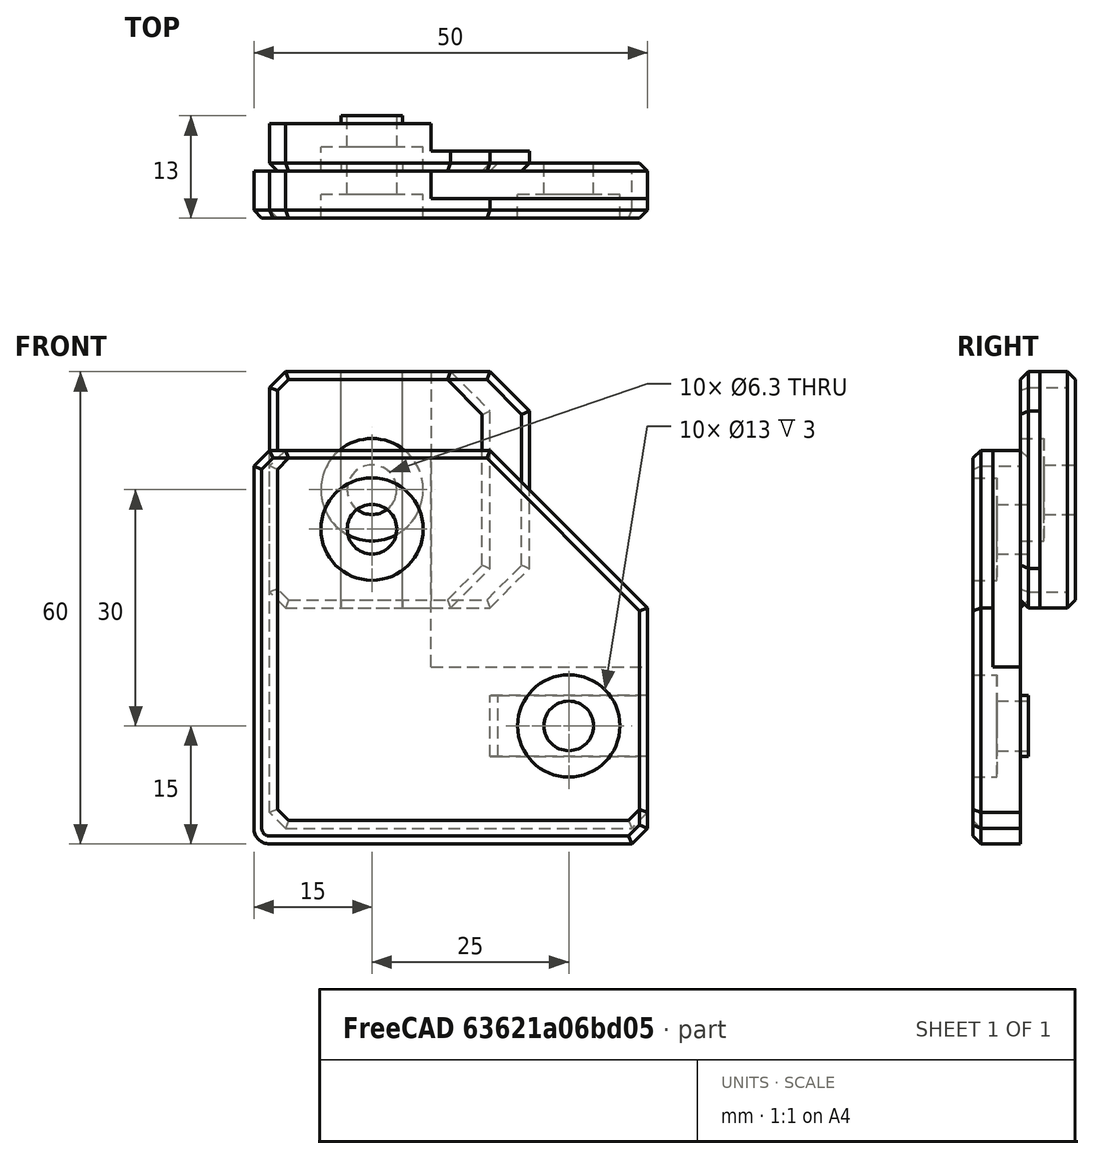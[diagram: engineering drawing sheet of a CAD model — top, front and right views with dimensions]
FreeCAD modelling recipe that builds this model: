
FCSTD DOCUMENT  (FreeCAD 0.19R24291 (Git))
Label: side-top-panel-clip
License: Other
LicenseURL: GPL3
objects: Part::Chamfer×14, Part::Box×11, Part::Cylinder×10, Part::MultiFuse×9, Part::Cut×9, Part::Feature×5, Part::Fillet×1, Part::Refine×1
note: 60 computed .brp shape members not serialized (recipe doc carries the construction recipe); baked Part::Feature solids carry a one-line shape summary decoded from their .brp

FEATURE [Part::Box] Box  label="Cube"
  AttacherType = Attacher::AttachEngine3D
  Height = 48
  Length = 48
  Placement = pos=(-28,-6,-28) rot=(0,0,1;0rad)
  Width = 6
FEATURE [Part::Box] Box001  label="Cube001"
  AttacherType = Attacher::AttachEngine3D
  Height = 20
  Length = 7.8
  Placement = pos=(-18.9,-1,0) rot=(0,0,1;0rad)
  Width = 2
FEATURE [Part::Chamfer] Chamfer
  Base = -> Box
  Edges = 1 edges r=20: [Edge6]
FEATURE [Part::Chamfer] Chamfer001
  Base = -> Chamfer
  Edges = 3 edges r=2: [Edge3,Edge11,Edge15]
FEATURE [Part::Chamfer] Chamfer002
  Base = -> Chamfer001
  Edges = 8 edges r=1: [Edge1,Edge5,Edge6,Edge7,Edge8,Edge9,Edge10,Edge11]
FEATURE [Part::Cylinder] Cylinder
  Angle = 360
  AttacherType = Attacher::AttachEngine3D
  Height = 10
  Placement = pos=(-15,-7,10) rot=(-1,0,0;1.5708rad)
  Radius = 3.15
FEATURE [Part::Cylinder] Cylinder001
  Angle = 360
  AttacherType = Attacher::AttachEngine3D
  Height = 10
  Placement = pos=(10,-7,-15) rot=(-1,0,0;1.5708rad)
  Radius = 3.15
FEATURE [Part::Box] Box002  label="Cube002"
  AttacherType = Attacher::AttachEngine3D
  Height = 7.8
  Length = 20
  Placement = pos=(0,-1,-18.9) rot=(0,0,1;0rad)
  Width = 2
FEATURE [Part::Chamfer] Chamfer003
  Base = -> Box001
  Edges = 2 edges r=1: [Edge11,Edge12]
FEATURE [Part::Chamfer] Chamfer004
  Base = -> Box002
  Edges = 2 edges r=1: [Edge3,Edge7]
FEATURE [Part::MultiFuse] Fusion
  Shapes = -> [Chamfer004,Chamfer003]
FEATURE [Part::MultiFuse] Fusion001
  Shapes = -> [Chamfer002,Fusion]
FEATURE [Part::Cylinder] Cylinder002
  Angle = 360
  AttacherType = Attacher::AttachEngine3D
  Height = 10
  Placement = pos=(10,-16,-15) rot=(-1,0,0;1.5708rad)
  Radius = 6.5
FEATURE [Part::Cylinder] Cylinder003
  Angle = 360
  AttacherType = Attacher::AttachEngine3D
  Height = 10
  Placement = pos=(-15,-16,10) rot=(-1,0,0;1.5708rad)
  Radius = 6.5
FEATURE [Part::MultiFuse] Fusion002
  Shapes = -> [Cylinder,Cylinder001]
FEATURE [Part::Cut] Cut
  Base = -> Fusion001
  Tool = -> Fusion002
FEATURE [Part::MultiFuse] Fusion003
  Placement = pos=(0,3,0) rot=(0,0,1;0rad)
  Shapes = -> [Cylinder003,Cylinder002]
FEATURE [Part::Cut] Cut001
  Base = -> Cut
  Tool = -> Fusion003
FEATURE [Part::Box] Box003  label="Cube003"
  AttacherType = Attacher::AttachEngine3D
  Height = 28
  Length = 28
  Placement = pos=(-7.5,-3.5,-7.5) rot=(0,0,1;0rad)
  Width = 16
FEATURE [Part::Feature] Cut002001  label="panel-mount001"
  shape: bbox 48 x 7 x 48 mm, 37 faces (baked)
FEATURE [Part::Box] Box004  label="Cube004"
  AttacherType = Attacher::AttachEngine3D
  Height = 30
  Length = 28
  Placement = pos=(-28,0,0) rot=(0,0,1;0rad)
  Width = 6
FEATURE [Part::Cylinder] Cylinder004
  Angle = 360
  AttacherType = Attacher::AttachEngine3D
  Height = 10
  Placement = pos=(-15,-7,15) rot=(-1,0,0;1.5708rad)
  Radius = 6.5
FEATURE [Part::Cylinder] Cylinder005
  Angle = 360
  AttacherType = Attacher::AttachEngine3D
  Height = 10
  Placement = pos=(-15,3e-15,15) rot=(-1,0,0;1.5708rad)
  Radius = 3.15
FEATURE [Part::Box] Box005  label="Cube005"
  AttacherType = Attacher::AttachEngine3D
  Height = 31
  Length = 16
  Placement = pos=(-7.5,2.5,0) rot=(0,0,1;0rad)
  Width = 9
FEATURE [Part::Box] Box006  label="Cube006"
  AttacherType = Attacher::AttachEngine3D
  Height = 30
  Length = 7.8
  Placement = pos=(-18.9,5,0) rot=(0,0,1;0rad)
  Width = 2
FEATURE [Part::Chamfer] Chamfer008
  Base = -> Box006
  Edges = 2 edges r=1: [Edge11,Edge12]
FEATURE [Part::Cylinder] Cylinder006
  Angle = 360
  AttacherType = Attacher::AttachEngine3D
  Height = 10
  Placement = pos=(10,-16,-15) rot=(-1,0,0;1.5708rad)
  Radius = 6.5
FEATURE [Part::Box] Box007  label="Cube007"
  AttacherType = Attacher::AttachEngine3D
  Height = 20
  Length = 7.8
  Placement = pos=(-18.9,-1,0) rot=(0,0,1;0rad)
  Width = 2
FEATURE [Part::Cylinder] Cylinder007
  Angle = 360
  AttacherType = Attacher::AttachEngine3D
  Height = 10
  Placement = pos=(-15,-16,10) rot=(-1,0,0;1.5708rad)
  Radius = 6.5
FEATURE [Part::Cylinder] Cylinder008
  Angle = 360
  AttacherType = Attacher::AttachEngine3D
  Height = 10
  Placement = pos=(-15,-7,10) rot=(-1,0,0;1.5708rad)
  Radius = 3.15
FEATURE [Part::Cylinder] Cylinder009
  Angle = 360
  AttacherType = Attacher::AttachEngine3D
  Height = 10
  Placement = pos=(10,-7,-15) rot=(-1,0,0;1.5708rad)
  Radius = 3.15
FEATURE [Part::Chamfer] Chamfer010
  Base = -> Box007
  Edges = 2 edges r=1: [Edge11,Edge12]
FEATURE [Part::Box] Box008  label="Cube008"
  AttacherType = Attacher::AttachEngine3D
  Height = 50
  Length = 50
  Placement = pos=(-30,-6,-30) rot=(0,0,1;0rad)
  Width = 6
FEATURE [Part::MultiFuse] Fusion005
  Shapes = -> [Cylinder008,Cylinder009]
FEATURE [Part::Box] Box009  label="Cube009"
  AttacherType = Attacher::AttachEngine3D
  Height = 7.8
  Length = 20
  Placement = pos=(0,-1,-18.9) rot=(0,0,1;0rad)
  Width = 2
FEATURE [Part::Box] Box010  label="Cube010"
  AttacherType = Attacher::AttachEngine3D
  Height = 28
  Length = 28
  Placement = pos=(-7.5,-3.5,-7.5) rot=(0,0,1;0rad)
  Width = 16
FEATURE [Part::MultiFuse] Fusion006
  Placement = pos=(0,3,0) rot=(0,0,1;0rad)
  Shapes = -> [Cylinder007,Cylinder006]
FEATURE [Part::Chamfer] Chamfer013
  Base = -> Box009
  Edges = 2 edges r=1: [Edge3,Edge7]
FEATURE [Part::MultiFuse] Fusion007
  Shapes = -> [Chamfer013,Chamfer010]
FEATURE [Part::Fillet] Fillet
  Base = -> Box008
  Edges = 1 edges r=2: [Edge4]
FEATURE [Part::Chamfer] Chamfer014
  Base = -> Fillet
  Edges = 1 edges r=20: [Edge12]
FEATURE [Part::Chamfer] Chamfer015
  Base = -> Chamfer014
  Edges = 2 edges r=2: [Edge8,Edge15]
FEATURE [Part::Cut] Cut002008002
  Base = -> Chamfer015
  Tool = -> Box010
FEATURE [Part::Chamfer] Chamfer016
  Base = -> Cut002008002
  Edges = 8 edges r=1: [Edge1,Edge2,Edge3,Edge4,Edge5,Edge6,Edge7,Edge8]
FEATURE [Part::MultiFuse] Fusion008
  Shapes = -> [Fusion007,Chamfer016]
FEATURE [Part::Cut] Cut002008003
  Base = -> Fusion008
  Tool = -> Fusion006
FEATURE [Part::Cut] Cut002008004  label="top-corner-clip"
  Base = -> Cut002008003
  Tool = -> Fusion005
FEATURE [Part::Cut] Cut002008006  label="side-corner-panel-clip"
  Base = -> Cut001
  Tool = -> Box003
FEATURE [Part::Feature] Cut002008006001  label="side-corner-panel-clip-smaller"
  shape: bbox 48 x 7 x 48 mm, 37 faces (baked)
FEATURE [Part::Feature] Cut002008005001  label="side-panel-clip001"
  shape: bbox 33 x 7 x 30 mm, 29 faces (baked)
FEATURE [Part::Feature] Cut002008004001  label="top-corner-clip001"
  shape: bbox 50 x 7 x 50 mm, 37 faces (baked)
FEATURE [Part::Cut] Cut002008006002
  Base = -> Box004
  Tool = -> Box005
FEATURE [Part::Chamfer] Chamfer017
  Base = -> Cut002008006002
  Edges = 2 edges r=5: [Edge11,Edge16]
FEATURE [Part::Chamfer] Chamfer018
  Base = -> Chamfer017
  Edges = 2 edges r=2: [Edge10,Edge14]
FEATURE [Part::Chamfer] Chamfer019
  Base = -> Chamfer018
  Edges = 8 edges r=1: [Edge1,Edge2,Edge3,Edge4,Edge5,Edge6,Edge7,Edge8]
FEATURE [Part::MultiFuse] Fusion009
  Shapes = -> [Chamfer008,Chamfer019]
FEATURE [Part::Cut] Cut002008006003
  Base = -> Fusion009
  Tool = -> Cylinder005
FEATURE [Part::Cut] Cut002008006004
  Base = -> Cut002008006003
  Tool = -> Cylinder004
FEATURE [Part::Refine] Cut002008006004001
  Source = -> Cut002008006004
FEATURE [Part::Feature] Cut002008006004001001  label="side-panel-clip-smaller"
  shape: bbox 28 x 7 x 30 mm, 29 faces (baked)
